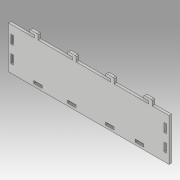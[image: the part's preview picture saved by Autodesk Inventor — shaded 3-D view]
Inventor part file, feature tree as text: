
AUTODESK INVENTOR PART (.ipt)
format: ipt  version: 2019.3 (Build 233278000, 278)  size: 188,416 bytes
history: native  units: mm
features: extrude x1, sketch x1
ambient origin geometry x8: Origin, YZ Plane, XZ Plane, XY Plane, X Axis, Y Axis, Z Axis, Center Point
bodies: Body1 (feature_tree)
feature tree (2):
  extrude  "Extrusion3"  Depth=50.0mm
  sketch  "Sketch1"  dims[d6=190.0mm d7=50.0mm d19=20.0mm d23=10.0mm d24=3.0mm d25=3.0mm d26=4.0mm d27=1.0mm d28=45.0mm d29=45.0mm d30=45.0mm d31=31.0mm d34=3.0mm d35=10.0mm d36=10.0mm d37=3.0mm d51=10.0mm d52=30.0mm d53=30.0mm d54=25.0mm d55=30.0mm d56=3.0mm d57=3.0mm d60=10.0mm d61=3.0mm d62=3.0mm d63=0.0mm]
